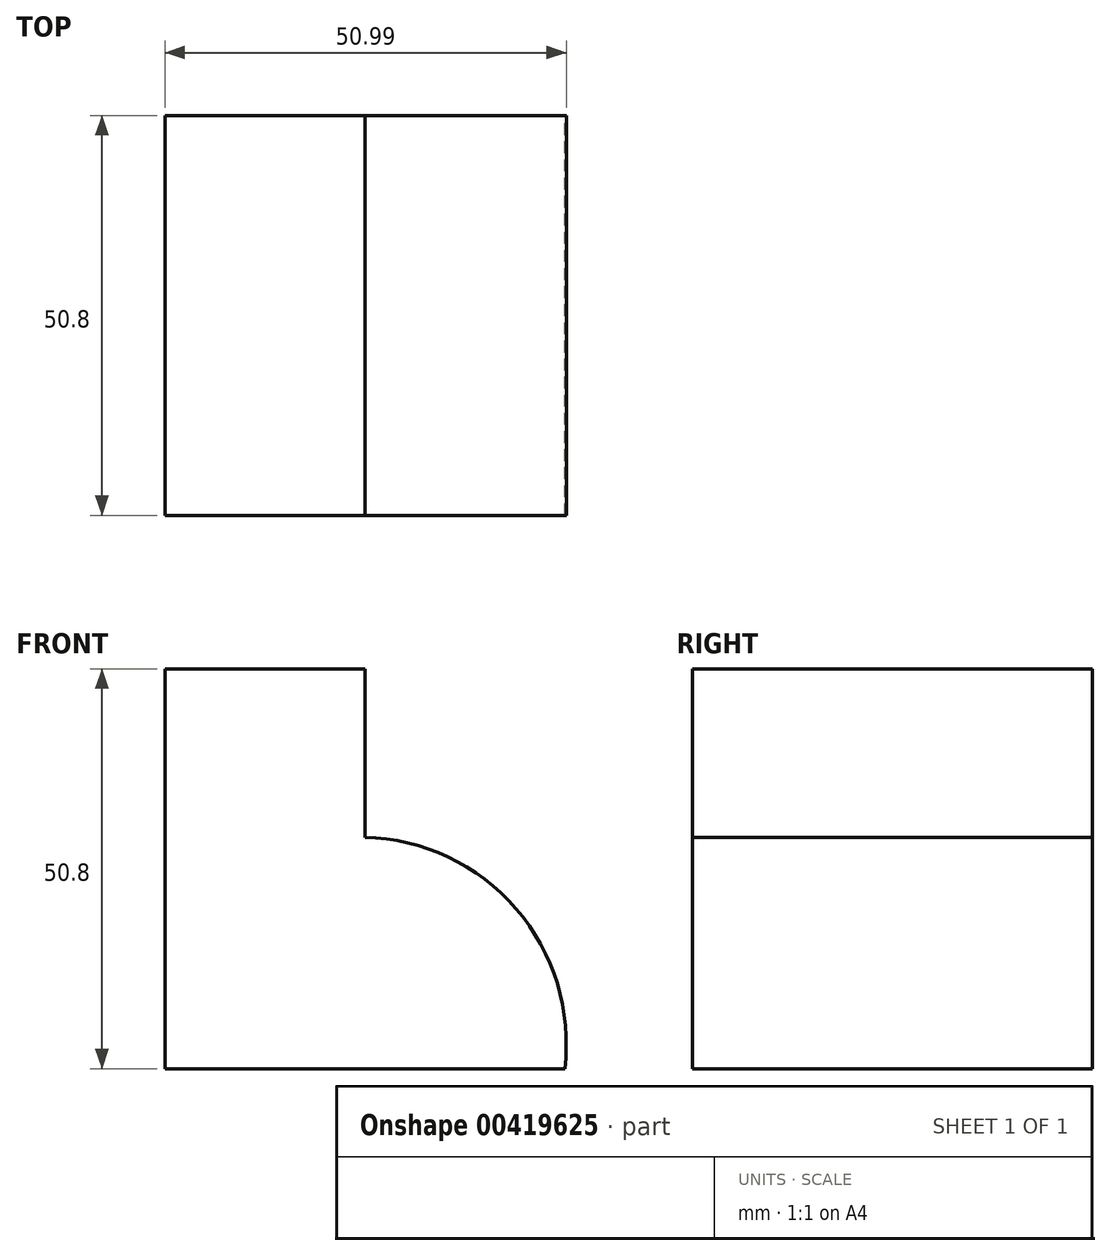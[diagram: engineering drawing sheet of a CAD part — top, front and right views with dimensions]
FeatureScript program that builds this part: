
annotation { "Feature Type Name" : "Feature", "Feature Type Description" : "" }
export const myFeature = defineFeature(function(context is Context, id is Id, definition is map)
    precondition{}
    {
        {
            var Q0;
            Q0=qCreatedBy(makeId("Front.planeOp"),FACE);
            var sketch = newSketch(context, id + "F0", { "sketchPlane" : qUnion([Q0])});
            skLineSegment(sketch, "E0", {"start": v(0, 0) * mm, "end": v(-50.8, 0) * mm});
            skLineSegment(sketch, "E1", {"start": v(-50.8, 0) * mm, "end": v(-50.8, 50.8) * mm});
            skLineSegment(sketch, "E2", {"start": v(-50.8, 50.8) * mm, "end": v(-25.4, 50.8) * mm});
            skLineSegment(sketch, "E3", {"start": v(-25.4, 50.8) * mm, "end": v(-25.4, 29.4) * mm});
            skArc(sketch, "E4", {"start": v(0, 0) * mm, "mid": v(-6.2, 20.32) * mm, "end": v(-25.4, 29.4) * mm});
            skSolve(sketch);
        }
        {
            var Q0;
            Q0=makeQuery(id+"F0.imprint","IMPRINT",FACE,{"disambiguationData":[TD([[makeQuery(id+"F0.imprint","IMPRINT",EDGE,{"derivedFrom":sQuery(id+"F0.wireOp",EDGE,"E0")}),-1.0]])]});
            extrude(context, id + "F1", {"entities" : qUnion([Q0]), "depth" : 50.8 * mm});
        }
    });
